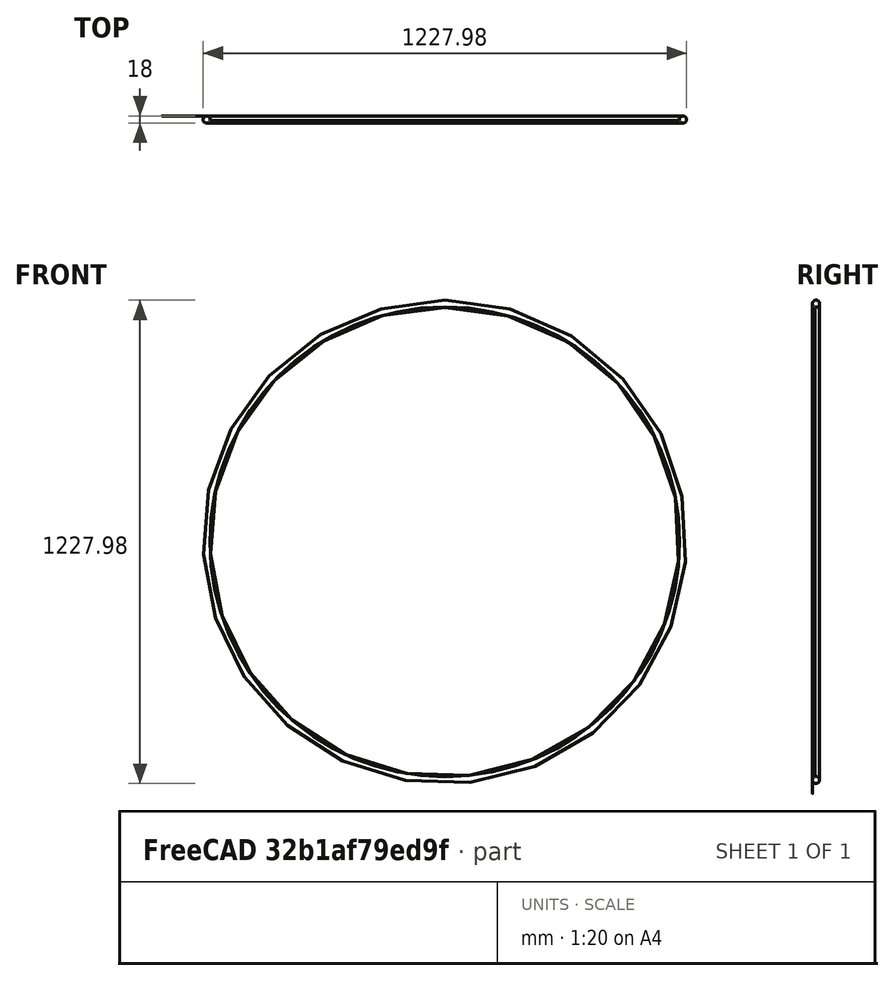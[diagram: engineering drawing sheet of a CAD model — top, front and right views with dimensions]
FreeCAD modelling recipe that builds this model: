
FCSTD DOCUMENT  (FreeCAD 0.18R16155 (Git))
Label: dish_with_rim
License: All rights reserved
LicenseURL: http://en.wikipedia.org/wiki/All_rights_reserved
objects: Sketcher::SketchObject×1, PartDesign::Revolution×1, PartDesign::Body×1, App::Part×1
note: 4 computed .brp shape members not serialized (recipe doc carries the construction recipe); baked Part::Feature solids carry a one-line shape summary decoded from their .brp

FEATURE [Sketcher::SketchObject] Sketch
  MapMode = 5
  Placement = pos=(0,0,0) rot=(0.57735,0.57735,0.57735;2.0944rad)
  Support = -> [YZ_Plane001]
  expr: Constraints[19] = Constraints.thickness
  sketch-geometry (13):
    g0: GeomPoint X=-479.981 Y=0 Z=0
    g1: ArcOfParabola CenterX=0 CenterY=0 CenterZ=0 NormalX=0 NormalY=0 NormalZ=1 Focal=479.981 AngleXU=-3.14159 StartAngle=-615 EndAngle=0
    g2: GeomPoint X=-479.981 Y=0 Z=0
    g3: LineSegment [constr] StartX=0 StartY=0 StartZ=0 EndX=-479.981 EndY=0 EndZ=0
    g4: Circle [constr] CenterX=-189.422 CenterY=619.855 CenterZ=0 NormalX=0 NormalY=0 NormalZ=1 AngleXU=0 Radius=9
    g5: GeomPoint X=-197 Y=615 Z=0
    g6: ArcOfParabola CenterX=2 CenterY=0 CenterZ=0 NormalX=0 NormalY=0 NormalZ=1 Focal=479.981 AngleXU=-3.14159 StartAngle=-611.498 EndAngle=0
    g7: GeomPoint X=-477.981 Y=0 Z=0
    g8: LineSegment [constr] StartX=2 StartY=0 StartZ=0 EndX=-477.981 EndY=0 EndZ=0
    g9: LineSegment StartX=0 StartY=0 StartZ=0 EndX=2 EndY=0 EndZ=0
    g10: GeomPoint X=-192.763 Y=611.498 Z=0
    g11: GeomPoint X=-192.763 Y=611.498 Z=0
    g12: ArcOfCircle CenterX=-189.422 CenterY=619.855 CenterZ=0 NormalX=0 NormalY=0 NormalZ=1 AngleXU=0 Radius=9 StartAngle=4.33205 EndAngle=9.99455
  constraints (30):
    c: PointOnObject(g0,g-1)
    c: InternalAlignment(g2,g1)
    c: Coincident(g2,g3)
    c: Coincident(g1,g3)
    c: Coincident(g2,g0)
    c: Coincident(g1,g-1)
    c: DistanceX(g0,g1) = 479.981
    c: DistanceY(g1,g1) = 615
    c: Horizontal(g1,g1)
    c: PointOnObject(g5,g4)
    c: Tangent(g1,g4,g5) = -1.5708
    c: Coincident(g5,g1)
    c: Diameter(g4) = 18
    c: PointOnObject(g6,g-1)
    c: InternalAlignment(g7,g6)
    c: Coincident(g7,g8)
    c: Coincident(g6,g8)
    c: PointOnObject(g7,g3)
    c: DistanceX(g1,g6) = 2  'thickness'
    c: DistanceX(g0,g7) = 2
    c: Horizontal(g6,g6)
    c: Coincident(g9,g1)
    c: Coincident(g9,g6)
    c: Coincident(g10,g11)
    c: Coincident(g10,g6)
    c: Coincident(g12,g4)
    c: Coincident(g12,g1)
    c: Coincident(g12,g6)
    c: DistanceX(g1,g1) = 197
    c: Distance(g1,g0) = 676.981
FEATURE [PartDesign::Revolution] Revolution
  Angle = 360
  Axis = (3e-16,1,-2e-16)
  Base = (0,0,0)
  Placement = pos=(0,0,0) rot=(0.57735,0.57735,0.57735;2.0944rad)
  Profile = -> Sketch
  ReferenceAxis = -> Sketch [H_Axis]
FEATURE [PartDesign::Body] Body  label="DishWithRim"
  Group = -> [Sketch,Revolution]
  Origin = -> Origin001
  Tip = -> Revolution
FEATURE [App::Part] Part
  Group = -> [Body]
  Origin = -> Origin
